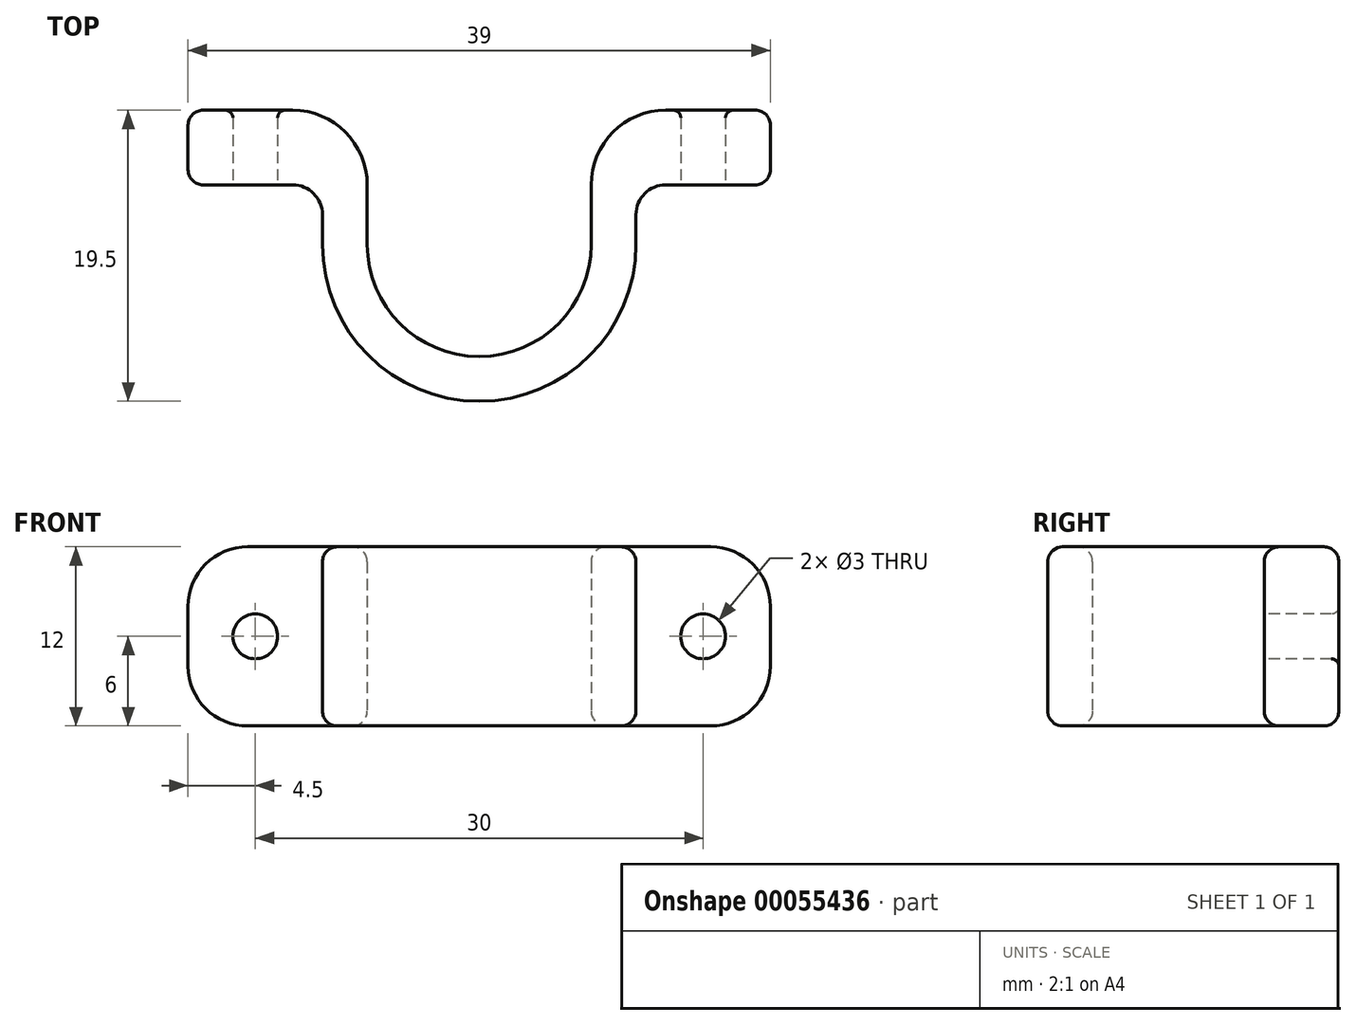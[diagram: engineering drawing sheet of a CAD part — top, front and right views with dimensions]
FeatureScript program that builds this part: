
annotation { "Feature Type Name" : "Feature", "Feature Type Description" : "" }
export const myFeature = defineFeature(function(context is Context, id is Id, definition is map)
    precondition{}
    {
        {
            var Q0;
            Q0=qCreatedBy(makeId("Top.planeOp"),FACE);
            var sketch = newSketch(context, id + "F0", { "sketchPlane" : qUnion([Q0])});
            skArc(sketch, "E0", {"start": v(0, -7.5) * mm, "mid": v(5.3, -5.3) * mm, "end": v(7.5, 0) * mm});
            skLineSegment(sketch, "E1", {"start": v(7.5, 9) * mm, "end": v(19.5, 9) * mm});
            skLineSegment(sketch, "E2", {"start": v(19.5, 9) * mm, "end": v(19.5, 4) * mm});
            skArc(sketch, "E3.0", {"start": v(0, -10.5) * mm, "mid": v(7.42, -7.42) * mm, "end": v(10.5, 0) * mm});
            skLineSegment(sketch, "E4", {"start": v(19.5, 4) * mm, "end": v(10.5, 4) * mm});
            skLineSegment(sketch, "E5", {"start": v(7.5, 0) * mm, "end": v(7.5, 9) * mm});
            skLineSegment(sketch, "E6", {"start": v(0, 38.29) * mm, "end": v(0, -44.91) * mm, "construction": true});
            skPoint(sketch, "E7.orphan", {"position": v(0, 7.5) * mm});
            skLineSegment(sketch, "E8", {"start": v(10.5, 0) * mm, "end": v(10.5, 4) * mm});
            skLineSegment(sketch, "E9", {"start": v(0, -7.5) * mm, "end": v(0, -10.5) * mm});
            skSolve(sketch);
        }
        {
            var Q0;
            Q0=makeQuery(id+"F0.imprint","IMPRINT",FACE,{"disambiguationData":[TD([[makeQuery(id+"F0.imprint","IMPRINT",EDGE,{"derivedFrom":sQuery(id+"F0.wireOp",EDGE,"E0")}),-1.0]])]});
            extrude(context, id + "F1", {"entities" : qUnion([Q0]), "depth" : 12 * mm});
        }
        {
            var Q0;
            Q0=makeQuery(id+"F1.opExtrude","SWEPT_FACE",FACE,{"disambiguationData":[OSD([sQuery(id+"F0.wireOp",EDGE,"E4")])]});
            var sketch = newSketch(context, id + "F2", { "sketchPlane" : qUnion([Q0])});
            skLineSegment(sketch, "E10", {"start": v(10.5, 12) * mm, "end": v(19.5, 0) * mm, "construction": true});
            skCircle(sketch, "E11", {"center": v(15, 6) * mm, "radius": 1.5 * mm});
            skSolve(sketch);
        }
        {
            var Q0;
            Q0=makeQuery(id+"F2.imprint","IMPRINT",FACE,{"disambiguationData":[TD([[makeQuery(id+"F2.imprint","IMPRINT",EDGE,{"derivedFrom":sQuery(id+"F2.wireOp",EDGE,"E11")}),1.0]])]});
            extrude(context, id + "F3", {"entities" : qUnion([Q0]), "operationType" : NewBodyOperationType.REMOVE, "endBound" : BoundingType.THROUGH_ALL, "oppositeDirection" : true, "depth" : 25 * mm});
        }
        {
            var Q0;
            Q0=makeQuery(id+"F1.opExtrude","SWEPT_EDGE",EDGE,{"disambiguationData":[OSD([sQuery(id+"F0.wireOp",EDGE,"E1"),sQuery(id+"F0.wireOp",EDGE,"E5")])]});
            fillet(context, id + "F4", {"entities" : qUnion([Q0]), "radius" : 5 * mm, "tangentPropagation" : true, "allowEdgeOverflow" : false});
        }
        {
            var Q0;
            Q0=makeQuery(id+"F1.opExtrude","SWEPT_EDGE",EDGE,{"disambiguationData":[OSD([sQuery(id+"F0.wireOp",EDGE,"E4"),sQuery(id+"F0.wireOp",EDGE,"E8")])]});
            fillet(context, id + "F5", {"entities" : qUnion([Q0]), "radius" : 2 * mm, "tangentPropagation" : true, "allowEdgeOverflow" : false});
        }
        {
            var Q0;
            Q0=makeQuery(id+"F1.opExtrude","CAP_EDGE",EDGE,{"disambiguationData":[OSD([sQuery(id+"F0.wireOp",EDGE,"E2")])],"isStart":true});
            var Q1;
            Q1=makeQuery(id+"F1.opExtrude","CAP_EDGE",EDGE,{"disambiguationData":[OSD([sQuery(id+"F0.wireOp",EDGE,"E2")])],"isStart":false});
            fillet(context, id + "F6", {"entities" : qUnion([Q0, Q1]), "radius" : 4 * mm, "tangentPropagation" : true, "allowEdgeOverflow" : false});
        }
        {
            var Q0;
            Q0=makeQuery(id+"F1.opExtrude","CAP_EDGE",EDGE,{"disambiguationData":[OSD([sQuery(id+"F0.wireOp",EDGE,"E3.0")])],"isStart":true});
            var Q1;
            {var subQ0=sQuery(id+"F0.wireOp",EDGE,"E5");var subQ1=sQuery(id+"F0.wireOp",EDGE,"E1");Q1=makeQuery(id+"F4.opFillet","BLEND_EDGE",EDGE,{"blendedFrom":[makeQuery(id+"F1.opExtrude","SWEPT_EDGE",EDGE,{"disambiguationData":[OSD([subQ1,subQ0])]}),makeQuery(id+"F1.opExtrude","CAP_FACE",FACE,{"disambiguationData":[OSD([sQuery(id+"F0.wireOp",EDGE,"E0"),subQ1,sQuery(id+"F0.wireOp",EDGE,"E2"),sQuery(id+"F0.wireOp",EDGE,"E3.0"),sQuery(id+"F0.wireOp",EDGE,"E4"),subQ0,sQuery(id+"F0.wireOp",EDGE,"E8"),sQuery(id+"F0.wireOp",EDGE,"E9")])],"isStart":true})],"blendedInto":[makeQuery(id+"F1.opExtrude","CAP_FACE",FACE,{"disambiguationData":[OSD([sQuery(id+"F0.wireOp",EDGE,"E0"),subQ1,sQuery(id+"F0.wireOp",EDGE,"E2"),sQuery(id+"F0.wireOp",EDGE,"E3.0"),sQuery(id+"F0.wireOp",EDGE,"E4"),subQ0,sQuery(id+"F0.wireOp",EDGE,"E8"),sQuery(id+"F0.wireOp",EDGE,"E9")])],"isStart":true})]});}
            fillet(context, id + "F7", {"entities" : qUnion([Q0, Q1]), "radius" : 1 * mm, "tangentPropagation" : true, "allowEdgeOverflow" : false});
        }
        {
            var Q0;
            Q0=makeQuery(id+"F3.boolean.opBoolean","COPY",EDGE,{"derivedFrom":makeQuery(id+"F3.opExtrude","CAP_EDGE",EDGE,{"disambiguationData":[OSD([sQuery(id+"F2.wireOp",EDGE,"E11")])],"isStart":true})});
            var Q1;
            Q1=makeQuery(id+"F3.boolean.opBoolean","INTERSECT",EDGE,{"derivedFrom":[makeQuery(id+"F1.opExtrude","SWEPT_FACE",FACE,{"disambiguationData":[OSD([sQuery(id+"F0.wireOp",EDGE,"E1")])]}),makeQuery(id+"F3.opExtrude","SWEPT_FACE",FACE,{"disambiguationData":[OSD([sQuery(id+"F2.wireOp",EDGE,"E11")])]})]});
            fillet(context, id + "F8", {"entities" : qUnion([Q0, Q1]), "radius" : 0.5 * mm, "tangentPropagation" : true, "allowEdgeOverflow" : false});
        }
        {
            var Q0;
            Q0=makeQuery(id+"F1.opExtrude","SWEPT_BODY",BODY,{"disambiguationData":[OSD([sQuery(id+"F0.wireOp",EDGE,"E0"),sQuery(id+"F0.wireOp",EDGE,"E1"),sQuery(id+"F0.wireOp",EDGE,"E2"),sQuery(id+"F0.wireOp",EDGE,"E3.0"),sQuery(id+"F0.wireOp",EDGE,"E4"),sQuery(id+"F0.wireOp",EDGE,"E5"),sQuery(id+"F0.wireOp",EDGE,"E8"),sQuery(id+"F0.wireOp",EDGE,"E9")])]});
            var Q1;
            Q1=makeQuery(id+"F1.opExtrude","SWEPT_FACE",FACE,{"disambiguationData":[OSD([sQuery(id+"F0.wireOp",EDGE,"E9")])]});
            mirror(context, id + "F9", {"operationType" : NewBodyOperationType.ADD, "entities" : qUnion([Q0]), "mirrorPlane" : qUnion([Q1])});
        }
    });
